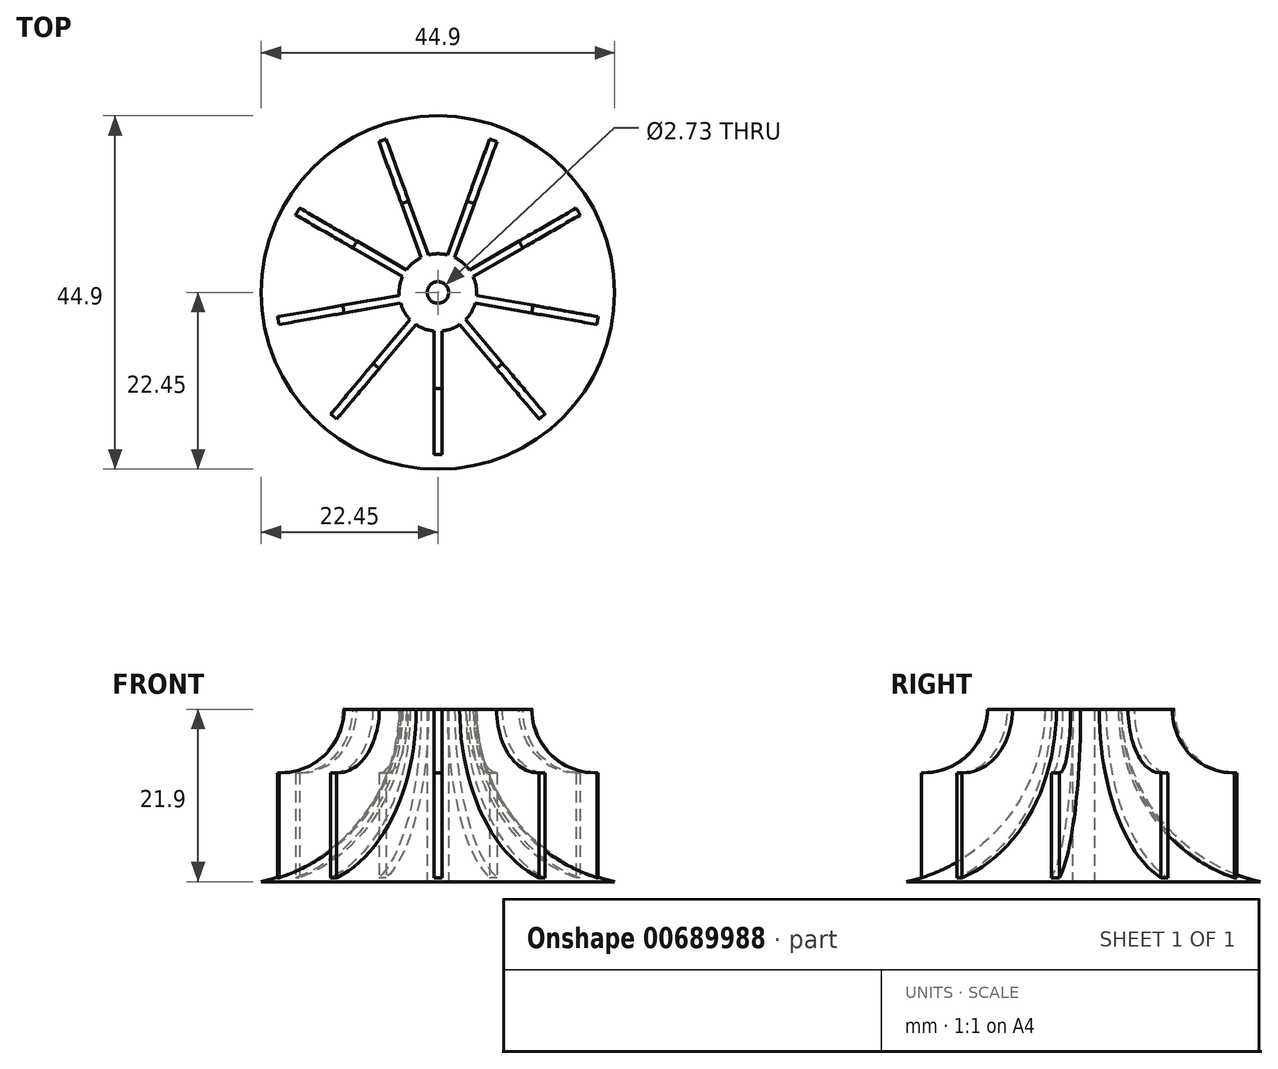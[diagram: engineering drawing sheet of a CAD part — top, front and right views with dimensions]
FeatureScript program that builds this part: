
annotation { "Feature Type Name" : "Feature", "Feature Type Description" : "" }
export const myFeature = defineFeature(function(context is Context, id is Id, definition is map)
    precondition{}
    {
        {
            var Q0;
            Q0=qCreatedBy(makeId("Front.planeOp"),FACE);
            var sketch = newSketch(context, id + "F0", { "sketchPlane" : qUnion([Q0])});
            skLineSegment(sketch, "E0", {"start": v(0, 0) * mm, "end": v(22.45, 0) * mm});
            skLineSegment(sketch, "E1", {"start": v(0, 0) * mm, "end": v(0, 21.9) * mm});
            skLineSegment(sketch, "E2", {"start": v(0, 21.9) * mm, "end": v(4.92, 21.9) * mm});
            skArc(sketch, "E3", {"start": v(4.92, 21.9) * mm, "mid": v(9.84, 7.87) * mm, "end": v(22.45, 0) * mm});
            skSolve(sketch);
        }
        {
            var Q0;
            Q0=makeQuery(id+"F0.imprint","IMPRINT",FACE,{"disambiguationData":[TD([[makeQuery(id+"F0.imprint","IMPRINT",EDGE,{"derivedFrom":sQuery(id+"F0.wireOp",EDGE,"E0")}),1.0]])]});
            var Q1;
            Q1=sQuery(id+"F0.wireOp",EDGE,"E1");
            revolve(context, id + "F1", {"entities" : qUnion([Q0]), "axis" : qUnion([Q1]), "revolveType" : RevolveType.FULL});
        }
        {
            var Q0;
            Q0=qCreatedBy(makeId("Top.planeOp"),FACE);
            var sketch = newSketch(context, id + "F2", { "sketchPlane" : qUnion([Q0])});
            skCircle(sketch, "E4", {"center": v(0, 0) * mm, "radius": 22.51 * mm});
            skSolve(sketch);
        }
        {
            var Q0;
            Q0=qCreatedBy(makeId("Top.planeOp"),FACE);
            var sketch = newSketch(context, id + "F3", { "sketchPlane" : qUnion([Q0])});
            skCircle(sketch, "E5", {"center": v(0, 0) * mm, "radius": 22.46 * mm});
            skCircle(sketch, "E6", {"center": v(0, 0) * mm, "radius": 3.27 * mm});
            skLineSegment(sketch, "E7.bottom", {"start": v(-0.5, -3.23) * mm, "end": v(0.5, -3.23) * mm});
            skLineSegment(sketch, "E7.top", {"start": v(-0.5, -20.58) * mm, "end": v(0.5, -20.58) * mm});
            skLineSegment(sketch, "E7.left", {"start": v(-0.5, -3.23) * mm, "end": v(-0.5, -20.58) * mm});
            skLineSegment(sketch, "E7.right", {"start": v(0.5, -3.23) * mm, "end": v(0.5, -20.58) * mm});
            skPoint(sketch, "E7.middle", {"position": v(0, -11.9) * mm});
            skLineSegment(sketch, "E8.1.0", {"start": v(2.46, -2.15) * mm, "end": v(13.6, -15.44) * mm});
            skLineSegment(sketch, "E8.1.1", {"start": v(1.7, -2.8) * mm, "end": v(12.84, -16.08) * mm});
            skLineSegment(sketch, "E8.1.2", {"start": v(12.84, -16.08) * mm, "end": v(13.6, -15.44) * mm});
            skLineSegment(sketch, "E8.1.3", {"start": v(1.7, -2.8) * mm, "end": v(2.46, -2.15) * mm});
            skLineSegment(sketch, "E8.2.0", {"start": v(3.27, -0.07) * mm, "end": v(20.35, -3.08) * mm});
            skLineSegment(sketch, "E8.2.1", {"start": v(3.1, -1.05) * mm, "end": v(20.18, -4.06) * mm});
            skLineSegment(sketch, "E8.2.2", {"start": v(20.18, -4.06) * mm, "end": v(20.35, -3.08) * mm});
            skLineSegment(sketch, "E8.2.3", {"start": v(3.1, -1.05) * mm, "end": v(3.27, -0.07) * mm});
            skLineSegment(sketch, "E9.2.3.0", {"start": v(2.55, 2.05) * mm, "end": v(17.57, 10.72) * mm});
            skLineSegment(sketch, "E9.3.3.0", {"start": v(3.04, 1.18) * mm, "end": v(18.07, 9.86) * mm});
            skLineSegment(sketch, "E9.6.3.0", {"start": v(18.07, 9.86) * mm, "end": v(17.57, 10.72) * mm});
            skLineSegment(sketch, "E9.9.3.0", {"start": v(3.04, 1.18) * mm, "end": v(2.55, 2.05) * mm});
            skLineSegment(sketch, "E9.2.4.0", {"start": v(0.63, 3.2) * mm, "end": v(6.57, 19.5) * mm});
            skLineSegment(sketch, "E9.3.4.0", {"start": v(1.57, 2.86) * mm, "end": v(7.5, 19.17) * mm});
            skLineSegment(sketch, "E9.6.4.0", {"start": v(7.5, 19.17) * mm, "end": v(6.57, 19.5) * mm});
            skLineSegment(sketch, "E9.9.4.0", {"start": v(1.57, 2.86) * mm, "end": v(0.63, 3.2) * mm});
            skLineSegment(sketch, "E9.2.5.0", {"start": v(-1.57, 2.86) * mm, "end": v(-7.5, 19.17) * mm});
            skLineSegment(sketch, "E9.3.5.0", {"start": v(-0.63, 3.2) * mm, "end": v(-6.57, 19.5) * mm});
            skLineSegment(sketch, "E9.6.5.0", {"start": v(-6.57, 19.5) * mm, "end": v(-7.5, 19.17) * mm});
            skLineSegment(sketch, "E9.9.5.0", {"start": v(-0.63, 3.2) * mm, "end": v(-1.57, 2.86) * mm});
            skLineSegment(sketch, "E9.2.6.0", {"start": v(-3.04, 1.18) * mm, "end": v(-18.07, 9.86) * mm});
            skLineSegment(sketch, "E9.3.6.0", {"start": v(-2.55, 2.05) * mm, "end": v(-17.57, 10.72) * mm});
            skLineSegment(sketch, "E9.6.6.0", {"start": v(-17.57, 10.72) * mm, "end": v(-18.07, 9.86) * mm});
            skLineSegment(sketch, "E9.9.6.0", {"start": v(-2.55, 2.05) * mm, "end": v(-3.04, 1.18) * mm});
            skLineSegment(sketch, "E9.2.7.0", {"start": v(-3.1, -1.05) * mm, "end": v(-20.18, -4.06) * mm});
            skLineSegment(sketch, "E9.3.7.0", {"start": v(-3.27, -0.07) * mm, "end": v(-20.35, -3.08) * mm});
            skLineSegment(sketch, "E9.6.7.0", {"start": v(-20.35, -3.08) * mm, "end": v(-20.18, -4.06) * mm});
            skLineSegment(sketch, "E9.9.7.0", {"start": v(-3.27, -0.07) * mm, "end": v(-3.1, -1.05) * mm});
            skLineSegment(sketch, "E9.2.8.0", {"start": v(-1.7, -2.8) * mm, "end": v(-12.84, -16.08) * mm});
            skLineSegment(sketch, "E9.3.8.0", {"start": v(-2.46, -2.15) * mm, "end": v(-13.6, -15.44) * mm});
            skLineSegment(sketch, "E9.6.8.0", {"start": v(-13.6, -15.44) * mm, "end": v(-12.84, -16.08) * mm});
            skLineSegment(sketch, "E9.9.8.0", {"start": v(-2.46, -2.15) * mm, "end": v(-1.7, -2.8) * mm});
            skSolve(sketch);
        }
        {
            var Q0;
            {var subQ1=sQuery(id+"F3.wireOp",EDGE,"E9.2.4.0");Q0=makeQuery(id+"F3.imprint","IMPRINT",FACE,{"disambiguationData":[TD([[makeQuery(id+"F3.imprint","IMPRINT",EDGE,{"derivedFrom":subQ1}),-1.0]])]});}
            var Q1;
            {var subQ1=sQuery(id+"F3.wireOp",EDGE,"E9.2.5.0");Q1=makeQuery(id+"F3.imprint","IMPRINT",FACE,{"disambiguationData":[TD([[makeQuery(id+"F3.imprint","IMPRINT",EDGE,{"derivedFrom":subQ1}),-1.0]])]});}
            var Q2;
            {var subQ1=sQuery(id+"F3.wireOp",EDGE,"E9.2.6.0");Q2=makeQuery(id+"F3.imprint","IMPRINT",FACE,{"disambiguationData":[TD([[makeQuery(id+"F3.imprint","IMPRINT",EDGE,{"derivedFrom":subQ1}),-1.0]])]});}
            var Q3;
            {var subQ1=sQuery(id+"F3.wireOp",EDGE,"E9.2.7.0");Q3=makeQuery(id+"F3.imprint","IMPRINT",FACE,{"disambiguationData":[TD([[makeQuery(id+"F3.imprint","IMPRINT",EDGE,{"derivedFrom":subQ1}),-1.0]])]});}
            var Q4;
            {var subQ1=sQuery(id+"F3.wireOp",EDGE,"E9.2.3.0");Q4=makeQuery(id+"F3.imprint","IMPRINT",FACE,{"disambiguationData":[TD([[makeQuery(id+"F3.imprint","IMPRINT",EDGE,{"derivedFrom":subQ1}),-1.0]])]});}
            var Q5;
            {var subQ1=sQuery(id+"F3.wireOp",EDGE,"E8.2.0");Q5=makeQuery(id+"F3.imprint","IMPRINT",FACE,{"disambiguationData":[TD([[makeQuery(id+"F3.imprint","IMPRINT",EDGE,{"derivedFrom":subQ1}),-1.0]])]});}
            var Q6;
            {var subQ1=sQuery(id+"F3.wireOp",EDGE,"E8.1.0");Q6=makeQuery(id+"F3.imprint","IMPRINT",FACE,{"disambiguationData":[TD([[makeQuery(id+"F3.imprint","IMPRINT",EDGE,{"derivedFrom":subQ1}),-1.0]])]});}
            var Q7;
            Q7=makeQuery(id+"F3.imprint","IMPRINT",FACE,{"disambiguationData":[TD([[makeQuery(id+"F3.imprint","IMPRINT",EDGE,{"derivedFrom":sQuery(id+"F3.wireOp",EDGE,"E7.top")}),1.0]])]});
            var Q8;
            {var subQ1=sQuery(id+"F3.wireOp",EDGE,"E9.2.8.0");Q8=makeQuery(id+"F3.imprint","IMPRINT",FACE,{"disambiguationData":[TD([[makeQuery(id+"F3.imprint","IMPRINT",EDGE,{"derivedFrom":subQ1}),-1.0]])]});}
            extrude(context, id + "F4", {"entities" : qUnion([Q0, Q1, Q2, Q3, Q4, Q5, Q6, Q7, Q8]), "operationType" : NewBodyOperationType.ADD, "depth" : 21.9 * mm, "offsetDistance" : 25 * mm});
        }
        {
            var Q0;
            Q0=qCreatedBy(makeId("Front.planeOp"),FACE);
            var sketch = newSketch(context, id + "F5", { "sketchPlane" : qUnion([Q0])});
            skLineSegment(sketch, "E10", {"start": v(0, 0) * mm, "end": v(0, 21.98) * mm});
            skLineSegment(sketch, "E11", {"start": v(0, 21.98) * mm, "end": v(-20.32, 21.98) * mm});
            skCircle(sketch, "E12", {"center": v(-20.32, 21.98) * mm, "radius": 8.14 * mm});
            skSolve(sketch);
        }
        {
            var Q0;
            Q0=makeQuery(id+"F5.imprint","IMPRINT",FACE,{"disambiguationData":[TD([[makeQuery(id+"F5.imprint","IMPRINT",EDGE,{"derivedFrom":sQuery(id+"F5.wireOp",EDGE,"E12")}),1.0]])]});
            var Q1;
            Q1=sQuery(id+"F5.wireOp",EDGE,"E10");
            revolve(context, id + "F6", {"operationType" : NewBodyOperationType.REMOVE, "surfaceOperationType" : NewSurfaceOperationType.NEW, "entities" : qUnion([Q0]), "axis" : qUnion([Q1]), "revolveType" : RevolveType.FULL, "oppositeDirection" : true});
        }
        {
            var Q0;
            Q0=makeQuery(id+"F2.imprint","IMPRINT",FACE,{"disambiguationData":[TD([[makeQuery(id+"F2.imprint","IMPRINT",EDGE,{"derivedFrom":sQuery(id+"F2.wireOp",EDGE,"E4")}),1.0]])]});
            var sketch = newSketch(context, id + "F7", { "sketchPlane" : qUnion([Q0])});
            skCircle(sketch, "E13", {"center": v(0, 0) * mm, "radius": 1.37 * mm});
            skSolve(sketch);
        }
        {
            var Q0;
            Q0 = qSketchRegion(id + "F7", true);
            extrude(context, id + "F8", {"entities" : qUnion([Q0]), "operationType" : NewBodyOperationType.REMOVE, "depth" : 30.9 * mm, "offsetDistance" : 25 * mm});
        }
    });
